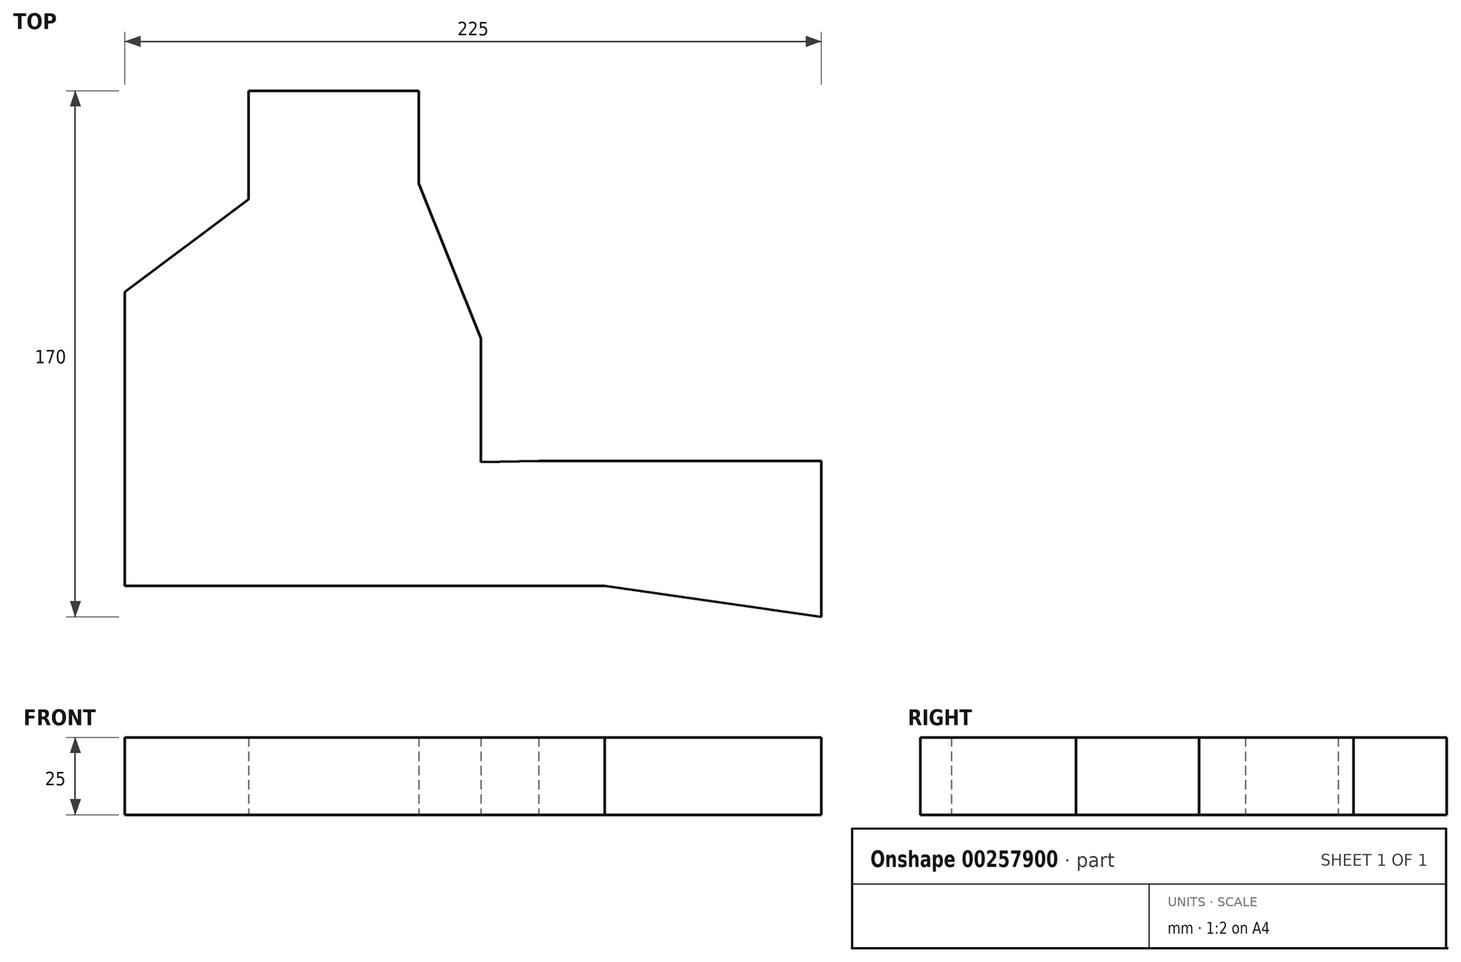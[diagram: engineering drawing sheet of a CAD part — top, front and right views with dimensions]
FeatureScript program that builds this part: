
annotation { "Feature Type Name" : "Feature", "Feature Type Description" : "" }
export const myFeature = defineFeature(function(context is Context, id is Id, definition is map)
    precondition{}
    {
        {
            var Q0;
            Q0=qCreatedBy(makeId("Top.planeOp"),FACE);
            var sketch = newSketch(context, id + "F0", { "sketchPlane" : qUnion([Q0])});
            skLineSegment(sketch, "E0", {"start": v(-101.3, 37.08) * mm, "end": v(-101.3, -57.92) * mm});
            skLineSegment(sketch, "E1", {"start": v(-101.3, -57.92) * mm, "end": v(53.7, -57.92) * mm});
            skLineSegment(sketch, "E2", {"start": v(-101.3, 37.08) * mm, "end": v(-61.3, 67.08) * mm});
            skLineSegment(sketch, "E3", {"start": v(-61.3, 67.08) * mm, "end": v(-61.3, 102.08) * mm});
            skLineSegment(sketch, "E4", {"start": v(-61.3, 102.08) * mm, "end": v(-6.3, 102.08) * mm});
            skLineSegment(sketch, "E5", {"start": v(-6.3, 102.08) * mm, "end": v(-6.3, 72.08) * mm});
            skLineSegment(sketch, "E6", {"start": v(53.7, -57.92) * mm, "end": v(123.7, -67.92) * mm});
            skLineSegment(sketch, "E7", {"start": v(123.7, -67.92) * mm, "end": v(123.7, -17.58) * mm});
            skLineSegment(sketch, "E8", {"start": v(123.7, -17.58) * mm, "end": v(32.45, -17.58) * mm});
            skLineSegment(sketch, "E9", {"start": v(-6.3, 72.08) * mm, "end": v(13.7, 22.08) * mm});
            skLineSegment(sketch, "E10", {"start": v(13.7, 22.08) * mm, "end": v(13.7, -17.92) * mm});
            skLineSegment(sketch, "E11", {"start": v(13.7, -17.92) * mm, "end": v(32.45, -17.58) * mm});
            skSolve(sketch);
        }
        {
            var Q0;
            Q0 = qSketchRegion(id + "F0", true);
            extrude(context, id + "F1", {"entities" : qUnion([Q0]), "depth" : 25 * mm});
        }
    });
